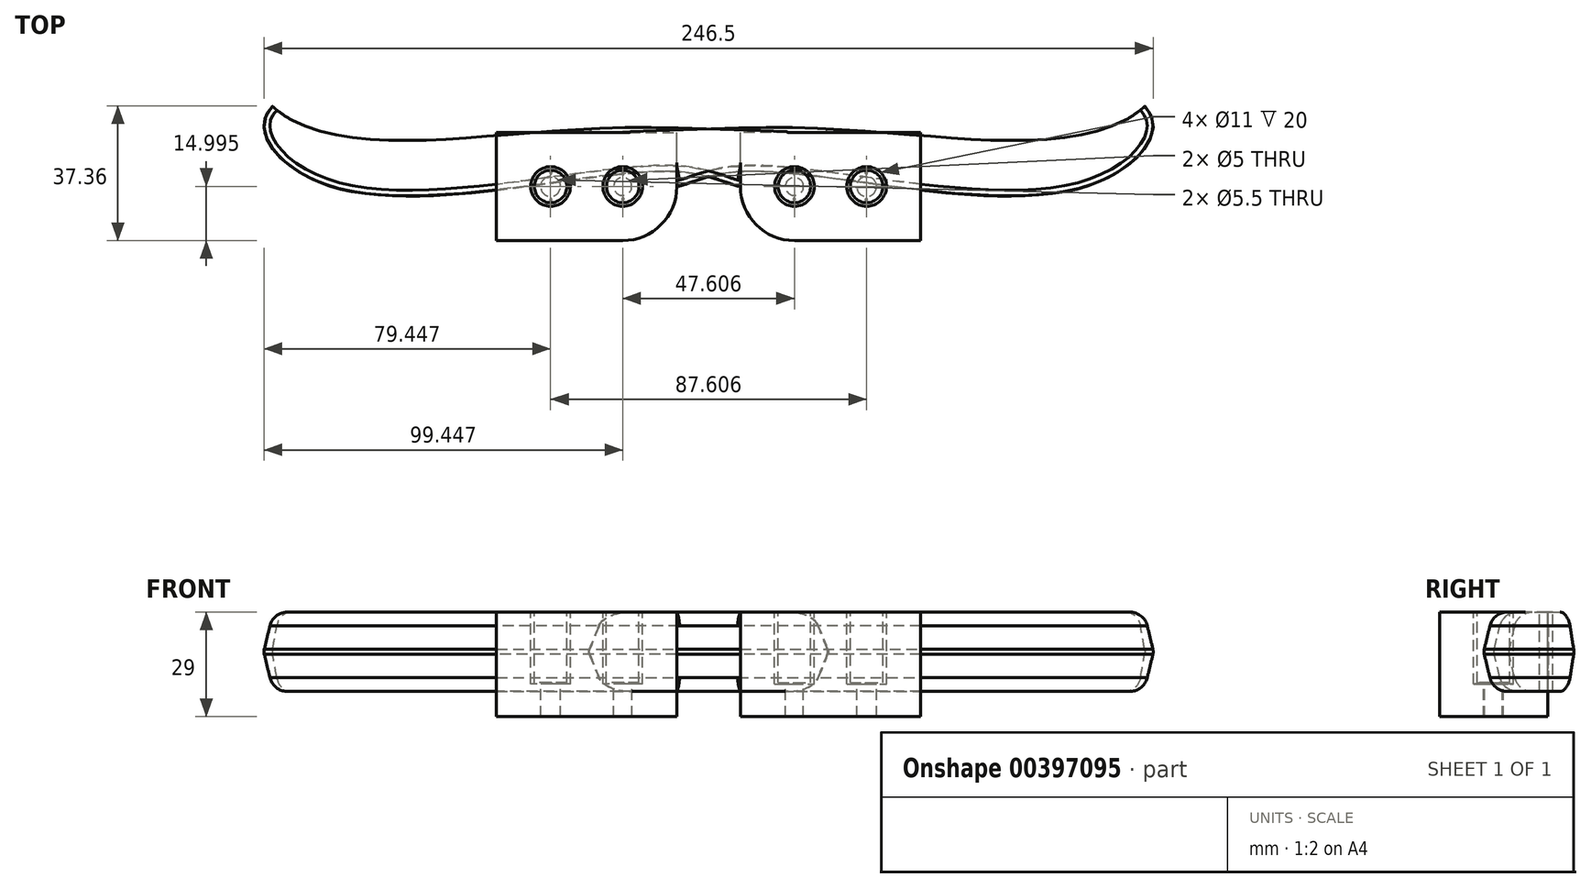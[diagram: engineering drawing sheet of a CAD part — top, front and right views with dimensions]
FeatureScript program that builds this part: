
annotation { "Feature Type Name" : "Feature", "Feature Type Description" : "" }
export const myFeature = defineFeature(function(context is Context, id is Id, definition is map)
    precondition{}
    {
        {
            var Q0;
            Q0=qCreatedBy(makeId("Top.planeOp"),FACE);
            var sketch = newSketch(context, id + "F0", { "sketchPlane" : qUnion([Q0])});
            skCircle(sketch, "E0", {"center": v(-43.8, 0.2) * mm, "radius": 2.5 * mm});
            skCircle(sketch, "E1", {"center": v(-23.8, 0.2) * mm, "radius": 2.5 * mm});
            skLineSegment(sketch, "E2", {"start": v(121.6, 32.7) * mm, "end": v(121.6, -14.8) * mm, "construction": true});
            skLineSegment(sketch, "E3", {"start": v(-33.4, 30.94) * mm, "end": v(-33.4, -22.47) * mm, "construction": true});
            skLineSegment(sketch, "E4", {"start": v(-58.8, -14.8) * mm, "end": v(119.38, -14.8) * mm, "construction": true});
            skLineSegment(sketch, "E5", {"start": v(8.55, 42.32) * mm, "end": v(8.55, -37.85) * mm, "construction": true});
            skFitSpline(sketch, "E6", {"points": [v(-8.8, 0.2) * mm, v(8.55, 4.21) * mm, v(104.23, 0) * mm, v(121.6, 21.85) * mm, v(8.55, 30.94) * mm, v(-33.4, 15.2) * mm], "startDerivative": vector(76.12, 0) * mm, "endDerivative": vector(-240.8, -177.9) * mm});
            skPoint(sketch, "E7", {"position": v(-33.8, 0.2) * mm});
            skLineSegment(sketch, "E8.bottom", {"start": v(-23.8, -14.8) * mm, "end": v(-58.8, -14.8) * mm});
            skLineSegment(sketch, "E8.top", {"start": v(-8.8, 15.2) * mm, "end": v(-58.8, 15.2) * mm});
            skLineSegment(sketch, "E8.left", {"start": v(-8.8, 0.2) * mm, "end": v(-8.8, 15.2) * mm});
            skLineSegment(sketch, "E8.right", {"start": v(-58.8, -14.8) * mm, "end": v(-58.8, 15.2) * mm});
            skPoint(sketch, "E9.visualSharp", {"position": v(-8.8, -14.8) * mm});
            skArc(sketch, "E9.filletArc", {"start": v(-23.8, -14.8) * mm, "mid": v(-13.2, -10.4) * mm, "end": v(-8.8, 0.2) * mm});
            skSolve(sketch);
        }
        {
            var Q0;
            Q0=qSketchRegion(id+"F0",true);
            extrude(context, id + "F1", {"entities" : qUnion([Q0]), "endBound" : BoundingType.SYMMETRIC, "depth" : 22 * mm, "hasDraft" : true, "draftAngle" : 13.5 * degree, "draftPullDirection" : true, "hasSecondDirectionDraft" : true, "secondDirectionDraftAngle" : 10 * degree, "secondDirectionDraftPullDirection" : true});
        }
        {
            var Q0;
            Q0=makeQuery(id+"F1.opExtrude","CAP_EDGE",EDGE,{"disambiguationData":[OSD([sQuery(id+"F0.wireOp",EDGE,"E6")])],"isStart":false});
            var Q1;
            Q1=makeQuery(id+"F1.opExtrude","CAP_EDGE",EDGE,{"disambiguationData":[OSD([sQuery(id+"F0.wireOp",EDGE,"E6")])],"isStart":true});
            fillet(context, id + "F2", {"entities" : qUnion([Q0, Q1]), "radius" : 5 * mm, "tangentPropagation" : true, "allowEdgeOverflow" : false});
        }
        {
            var Q0;
            Q0=qCreatedBy(makeId("Top.planeOp"),FACE);
            var sketch = newSketch(context, id + "F3", { "sketchPlane" : qUnion([Q0])});
            skCircle(sketch, "E10.0", {"center": v(-43.8, 0.2) * mm, "radius": 2.5 * mm});
            skCircle(sketch, "E11.0", {"center": v(-23.8, 0.2) * mm, "radius": 2.5 * mm});
            skPoint(sketch, "E12.0", {"position": v(-58.8, 15.2) * mm});
            skPoint(sketch, "E13.0", {"position": v(-58.8, -14.8) * mm});
            skLineSegment(sketch, "E14.bottom", {"start": v(-58.8, 15.2) * mm, "end": v(-8.8, 15.2) * mm});
            skLineSegment(sketch, "E14.top", {"start": v(-58.8, -14.8) * mm, "end": v(-23.8, -14.8) * mm});
            skLineSegment(sketch, "E14.left", {"start": v(-58.8, 15.2) * mm, "end": v(-58.8, -14.8) * mm});
            skLineSegment(sketch, "E14.right", {"start": v(-8.8, 15.2) * mm, "end": v(-8.8, 0.2) * mm});
            skPoint(sketch, "E15.visualSharp", {"position": v(-8.8, -14.8) * mm});
            skArc(sketch, "E15.filletArc", {"start": v(-23.8, -14.8) * mm, "mid": v(-13.2, -10.4) * mm, "end": v(-8.8, 0.2) * mm});
            skCircle(sketch, "E16", {"center": v(-43.8, 0.2) * mm, "radius": 2.75 * mm});
            skSolve(sketch);
        }
        {
            var Q0;
            Q0=qSketchRegion(id+"F3",true);
            extrude(context, id + "F4", {"entities" : qUnion([Q0]), "operationType" : NewBodyOperationType.ADD, "endBound" : BoundingType.SYMMETRIC, "oppositeDirection" : true, "depth" : 22 * mm});
        }
        {
            var Q0;
            Q0=makeQuery(id+"F4.boolean.opBoolean","MERGE",FACE,{"derivedFrom":[makeQuery(id+"F1.opExtrude","CAP_FACE",FACE,{"disambiguationData":[OSD([sQuery(id+"F0.wireOp",EDGE,"E0"),sQuery(id+"F0.wireOp",EDGE,"E1"),sQuery(id+"F0.wireOp",EDGE,"E6"),sQuery(id+"F0.wireOp",EDGE,"E8.bottom"),sQuery(id+"F0.wireOp",EDGE,"E8.top"),sQuery(id+"F0.wireOp",EDGE,"E8.right"),sQuery(id+"F0.wireOp",EDGE,"E9.filletArc")])],"isStart":false}),makeQuery(id+"F4.opExtrude","CAP_FACE",FACE,{"disambiguationData":[OSD([sQuery(id+"F3.wireOp",EDGE,"E11.0"),sQuery(id+"F3.wireOp",EDGE,"E14.bottom"),sQuery(id+"F3.wireOp",EDGE,"E14.top"),sQuery(id+"F3.wireOp",EDGE,"E14.left"),sQuery(id+"F3.wireOp",EDGE,"E14.right"),sQuery(id+"F3.wireOp",EDGE,"E15.filletArc"),sQuery(id+"F3.wireOp",EDGE,"E16")])],"isStart":true})]});
            var sketch = newSketch(context, id + "F5", { "sketchPlane" : qUnion([Q0])});
            skCircle(sketch, "E17", {"center": v(-43.8, 0.2) * mm, "radius": 5.5 * mm});
            skCircle(sketch, "E18", {"center": v(-23.8, 0.2) * mm, "radius": 5.5 * mm});
            skSolve(sketch);
        }
        {
            var Q0;
            Q0=qSketchRegion(id+"F5",true);
            extrude(context, id + "F6", {"entities" : qUnion([Q0]), "operationType" : NewBodyOperationType.REMOVE, "oppositeDirection" : true, "depth" : 20 * mm});
        }
        {
            var Q0;
            {var subQ0=makeQuery(id+"F1.opExtrude","SWEPT_FACE",FACE,{"disambiguationData":[OSD([sQuery(id+"F0.wireOp",EDGE,"E6")])]});Q0=makeQuery(id+"F1.*.booleanUnion.opBoolean","MERGE",EDGE,{"derivedFrom":[makeQuery(id+"F1.*.split.splitOp","SPLIT_SURFACE_INTERSECT",EDGE,{"derivedFrom":[subQ0]}),makeQuery(id+"F1.*.split.splitOp","SPLIT_SURFACE_INTERSECT",EDGE,{"derivedFrom":[subQ0],"isFromBackBody":true})]});}
            fillet(context, id + "F7", {"entities" : qUnion([Q0]), "radius" : 2.9 * mm, "tangentPropagation" : true, "allowEdgeOverflow" : false});
        }
        {
            var Q0;
            Q0=qCreatedBy(makeId("Top.planeOp"),FACE);
            var sketch = newSketch(context, id + "F8", { "sketchPlane" : qUnion([Q0])});
            skFitSpline(sketch, "E19", {"points": [v(-46.12, 18.18) * mm, v(14.83, 16.57) * mm, v(81.68, 12.97) * mm, v(117.59, 19.86) * mm, v(123.24, 32.51) * mm, v(-11.72, 37.93) * mm, v(-46.12, 18.18) * mm]});
            skSolve(sketch);
        }
        {
            var Q0;
            Q0=qSketchRegion(id+"F8",true);
            extrude(context, id + "F9", {"entities" : qUnion([Q0]), "operationType" : NewBodyOperationType.REMOVE, "endBound" : BoundingType.SYMMETRIC, "oppositeDirection" : true, "depth" : 30 * mm});
        }
        {
            var Q0;
            Q0=makeQuery(id+"F4.boolean.opBoolean","MERGE",FACE,{"derivedFrom":[makeQuery(id+"F1.opExtrude","CAP_FACE",FACE,{"disambiguationData":[OSD([sQuery(id+"F0.wireOp",EDGE,"E0"),sQuery(id+"F0.wireOp",EDGE,"E1"),sQuery(id+"F0.wireOp",EDGE,"E6"),sQuery(id+"F0.wireOp",EDGE,"E8.bottom"),sQuery(id+"F0.wireOp",EDGE,"E8.top"),sQuery(id+"F0.wireOp",EDGE,"E8.right"),sQuery(id+"F0.wireOp",EDGE,"E9.filletArc")])],"isStart":false}),makeQuery(id+"F4.opExtrude","CAP_FACE",FACE,{"disambiguationData":[OSD([sQuery(id+"F3.wireOp",EDGE,"E11.0"),sQuery(id+"F3.wireOp",EDGE,"E14.bottom"),sQuery(id+"F3.wireOp",EDGE,"E14.top"),sQuery(id+"F3.wireOp",EDGE,"E14.left"),sQuery(id+"F3.wireOp",EDGE,"E14.right"),sQuery(id+"F3.wireOp",EDGE,"E15.filletArc"),sQuery(id+"F3.wireOp",EDGE,"E16")])],"isStart":true})]});
            var sketch = newSketch(context, id + "F10", { "sketchPlane" : qUnion([Q0])});
            skCircle(sketch, "E20.0", {"center": v(-43.8, 0.2) * mm, "radius": 5.5 * mm, "construction": true});
            skCircle(sketch, "E21.0", {"center": v(-23.8, 0.2) * mm, "radius": 5.5 * mm, "construction": true});
            skCircle(sketch, "E22.0", {"center": v(-23.8, 0.2) * mm, "radius": 4.5 * mm});
            skCircle(sketch, "E23.0", {"center": v(-43.8, 0.2) * mm, "radius": 4.5 * mm});
            skSolve(sketch);
        }
        {
            var Q0;
            Q0=qSketchRegion(id+"F10",true);
            extrude(context, id + "F11", {"entities" : qUnion([Q0]), "operationType" : NewBodyOperationType.ADD, "oppositeDirection" : true, "depth" : 19.5 * mm});
        }
        {
            var Q0;
            Q0=makeQuery(id+"F6.boolean.opBoolean","COPY",FACE,{"derivedFrom":makeQuery(id+"F6.opExtrude","CAP_FACE",FACE,{"disambiguationData":[OSD([sQuery(id+"F5.wireOp",EDGE,"E17")])],"isStart":false})});
            var sketch = newSketch(context, id + "F12", { "sketchPlane" : qUnion([Q0])});
            skCircle(sketch, "E24", {"center": v(-43.73, 3.93) * mm, "radius": 0.3 * mm});
            skCircle(sketch, "E25", {"center": v(-23.74, 3.77) * mm, "radius": 0.3 * mm});
            skCircle(sketch, "E26", {"center": v(-23.74, -3.28) * mm, "radius": 0.3 * mm});
            skCircle(sketch, "E27", {"center": v(-43.73, -3.44) * mm, "radius": 0.3 * mm});
            skSolve(sketch);
        }
        {
            var Q0;
            Q0=qSketchRegion(id+"F12",true);
            extrude(context, id + "F13", {"entities" : qUnion([Q0]), "operationType" : NewBodyOperationType.ADD, "depth" : 5 * mm});
        }
        {
            var Q0;
            Q0=makeQuery(id+"F4.boolean.opBoolean","MERGE",FACE,{"derivedFrom":[makeQuery(id+"F1.opExtrude","CAP_FACE",FACE,{"disambiguationData":[OSD([sQuery(id+"F0.wireOp",EDGE,"E0"),sQuery(id+"F0.wireOp",EDGE,"E1"),sQuery(id+"F0.wireOp",EDGE,"E6"),sQuery(id+"F0.wireOp",EDGE,"E8.bottom"),sQuery(id+"F0.wireOp",EDGE,"E8.top"),sQuery(id+"F0.wireOp",EDGE,"E8.right"),sQuery(id+"F0.wireOp",EDGE,"E9.filletArc")])],"isStart":true}),makeQuery(id+"F4.opExtrude","CAP_FACE",FACE,{"disambiguationData":[OSD([sQuery(id+"F3.wireOp",EDGE,"E11.0"),sQuery(id+"F3.wireOp",EDGE,"E14.bottom"),sQuery(id+"F3.wireOp",EDGE,"E14.top"),sQuery(id+"F3.wireOp",EDGE,"E14.left"),sQuery(id+"F3.wireOp",EDGE,"E14.right"),sQuery(id+"F3.wireOp",EDGE,"E15.filletArc"),sQuery(id+"F3.wireOp",EDGE,"E16")])],"isStart":false})]});
            var sketch = newSketch(context, id + "F14", { "sketchPlane" : qUnion([Q0])});
            skLineSegment(sketch, "E28.0", {"start": v(-58.8, 14.8) * mm, "end": v(-23.8, 14.8) * mm});
            skLineSegment(sketch, "E29.0", {"start": v(-58.8, -15.2) * mm, "end": v(-58.8, 14.8) * mm});
            skLineSegment(sketch, "E30.0", {"start": v(-58.8, -15.2) * mm, "end": v(-21.93, -15.2) * mm});
            skArc(sketch, "E31.0", {"start": v(-23.8, 14.8) * mm, "mid": v(-13.2, 10.4) * mm, "end": v(-8.8, -0.2) * mm});
            skLineSegment(sketch, "E32.0", {"start": v(-8.8, -6.84) * mm, "end": v(-8.8, -0.2) * mm});
            skLineSegment(sketch, "E33", {"start": v(-8.8, -6.84) * mm, "end": v(-8.8, -15.2) * mm});
            skLineSegment(sketch, "E34", {"start": v(-8.8, -15.2) * mm, "end": v(-21.93, -15.2) * mm});
            skCircle(sketch, "E35.0", {"center": v(-23.8, -0.2) * mm, "radius": 2.5 * mm});
            skCircle(sketch, "E36.0", {"center": v(-43.8, -0.2) * mm, "radius": 2.75 * mm});
            skSolve(sketch);
        }
        {
            var Q0;
            Q0=qSketchRegion(id+"F14",true);
            extrude(context, id + "F15", {"entities" : qUnion([Q0]), "operationType" : NewBodyOperationType.ADD, "depth" : 7 * mm});
        }
        {
            var Q0;
            Q0=makeQuery(id+"F1.*.split.splitOp","SPLIT",BODY,{"derivedFrom":makeQuery(id+"F1.opExtrude","SWEPT_BODY",BODY,{"disambiguationData":[OSD([sQuery(id+"F0.wireOp",EDGE,"E0"),sQuery(id+"F0.wireOp",EDGE,"E1"),sQuery(id+"F0.wireOp",EDGE,"E6"),sQuery(id+"F0.wireOp",EDGE,"E8.bottom"),sQuery(id+"F0.wireOp",EDGE,"E8.top"),sQuery(id+"F0.wireOp",EDGE,"E8.right"),sQuery(id+"F0.wireOp",EDGE,"E9.filletArc")])]})});
            var Q1;
            Q1=qCreatedBy(makeId("Right.planeOp"),FACE);
            mirror(context, id + "F16", {"entities" : qUnion([Q0]), "mirrorPlane" : qUnion([Q1])});
        }
    });
